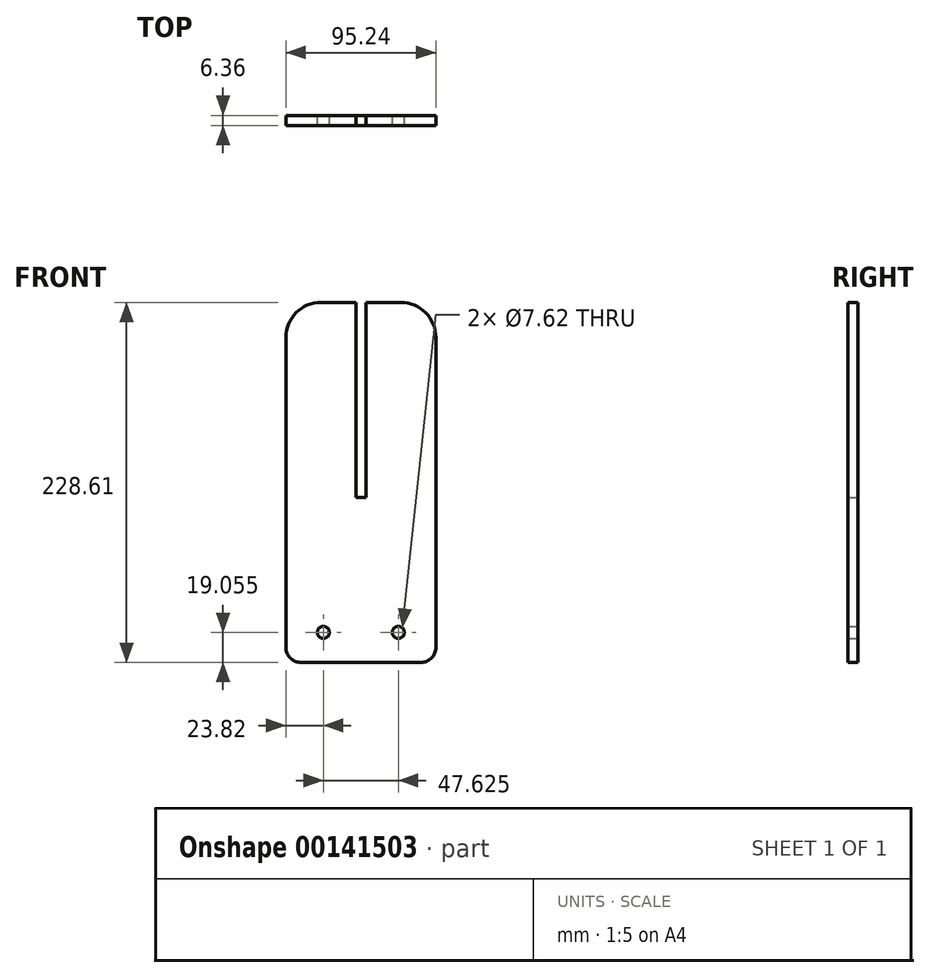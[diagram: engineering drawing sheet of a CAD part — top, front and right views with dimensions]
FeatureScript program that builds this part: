
annotation { "Feature Type Name" : "Feature", "Feature Type Description" : "" }
export const myFeature = defineFeature(function(context is Context, id is Id, definition is map)
    precondition{}
    {
        {
            var Q0;
            Q0=qCreatedBy(makeId("Front.planeOp"),FACE);
            var sketch = newSketch(context, id + "F0", { "sketchPlane" : qUnion([Q0])});
            skLineSegment(sketch, "E0.bottom", {"start": v(-25.4, 123.83) * mm, "end": v(-3.18, 123.83) * mm});
            skLineSegment(sketch, "E0.top", {"start": v(-38.1, -104.78) * mm, "end": v(38.1, -104.78) * mm});
            skLineSegment(sketch, "E0.left", {"start": v(-47.63, 101.6) * mm, "end": v(-47.63, -95.25) * mm});
            skLineSegment(sketch, "E0.right", {"start": v(47.62, 101.6) * mm, "end": v(47.62, -95.25) * mm});
            skPoint(sketch, "E0.middle", {"position": v(0, 0) * mm});
            skPoint(sketch, "E1.visualSharp", {"position": v(-47.63, 123.83) * mm});
            skArc(sketch, "E1.filletArc", {"start": v(-25.4, 123.83) * mm, "mid": v(-41.12, 117.32) * mm, "end": v(-47.63, 101.6) * mm});
            skPoint(sketch, "E2.visualSharp", {"position": v(47.62, 123.83) * mm});
            skArc(sketch, "E2.filletArc", {"start": v(47.62, 101.6) * mm, "mid": v(41.12, 117.32) * mm, "end": v(25.4, 123.83) * mm});
            skPoint(sketch, "E3.visualSharp", {"position": v(-47.63, -104.78) * mm});
            skArc(sketch, "E3.filletArc", {"start": v(-47.63, -95.25) * mm, "mid": v(-44.84, -101.99) * mm, "end": v(-38.1, -104.78) * mm});
            skPoint(sketch, "E4.visualSharp", {"position": v(47.63, -104.78) * mm});
            skArc(sketch, "E4.filletArc", {"start": v(38.1, -104.78) * mm, "mid": v(44.84, -101.99) * mm, "end": v(47.63, -95.25) * mm});
            skLineSegment(sketch, "E5", {"start": v(3.18, 0) * mm, "end": v(0, 0) * mm});
            skLineSegment(sketch, "E6", {"start": v(3.18, 0) * mm, "end": v(3.18, 123.83) * mm});
            skLineSegment(sketch, "E7.MirrorCS", {"start": v(-3.18, 0) * mm, "end": v(-3.18, 123.83) * mm});
            skLineSegment(sketch, "E8.MirrorCS", {"start": v(-3.18, 0) * mm, "end": v(0, 0) * mm});
            skLineSegment(sketch, "E9.trimOffspring", {"start": v(3.18, 123.83) * mm, "end": v(25.4, 123.83) * mm});
            skCircle(sketch, "E10", {"center": v(-23.8, -85.73) * mm, "radius": 3.81 * mm});
            skCircle(sketch, "E11", {"center": v(23.83, -85.73) * mm, "radius": 3.81 * mm});
            skSolve(sketch);
        }
        {
            var Q0;
            Q0 = qSketchRegion(id + "F0", true);
            extrude(context, id + "F1", {"entities" : qUnion([Q0]), "endBound" : BoundingType.SYMMETRIC, "depth" : 6.35 * mm});
        }
    });
